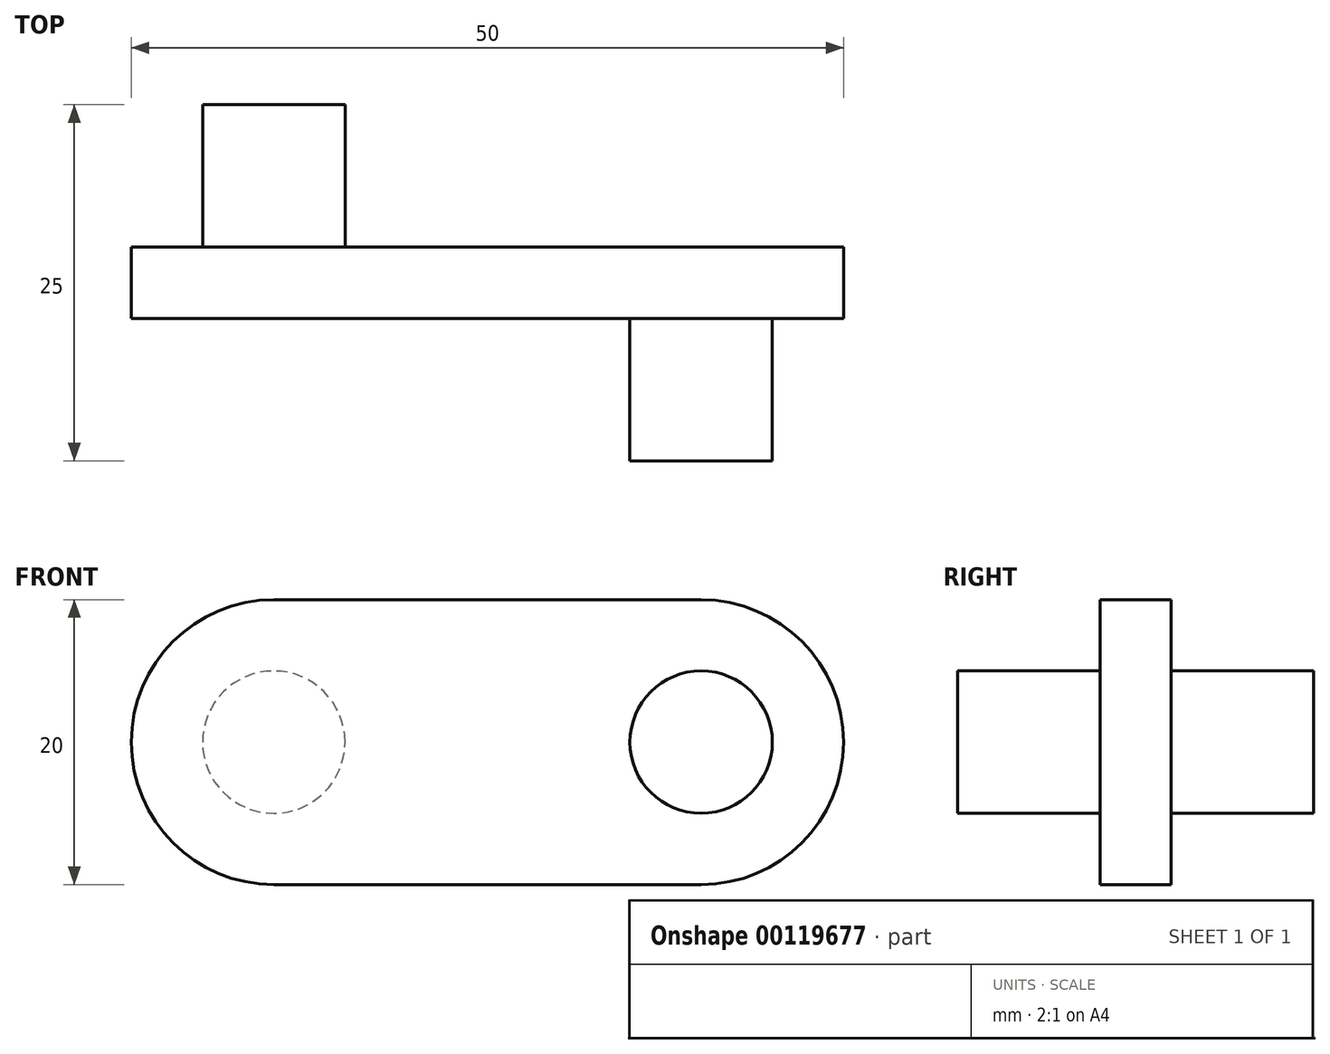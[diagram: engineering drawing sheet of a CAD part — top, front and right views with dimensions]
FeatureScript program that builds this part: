
annotation { "Feature Type Name" : "Feature", "Feature Type Description" : "" }
export const myFeature = defineFeature(function(context is Context, id is Id, definition is map)
    precondition{}
    {
        {
            var Q0;
            Q0=qCreatedBy(makeId("Front.planeOp"),FACE);
            var sketch = newSketch(context, id + "F0", { "sketchPlane" : qUnion([Q0])});
            skArc(sketch, "E0", {"start": v(0, 10) * mm, "mid": v(-10, 0) * mm, "end": v(0, -10) * mm});
            skLineSegment(sketch, "E1", {"start": v(0, 10) * mm, "end": v(30, 10) * mm});
            skLineSegment(sketch, "E2", {"start": v(0, -10) * mm, "end": v(30, -10) * mm});
            skArc(sketch, "E3", {"start": v(30, 10) * mm, "mid": v(40, 0) * mm, "end": v(30, -10) * mm});
            skSolve(sketch);
        }
        {
            var Q0;
            Q0=qSketchRegion(id+"F0",true);
            extrude(context, id + "F1", {"entities" : qUnion([Q0]), "endBound" : BoundingType.SYMMETRIC, "depth" : 5 * mm});
        }
        {
            var Q0;
            Q0=makeQuery(id+"F1.opExtrude","CAP_FACE",FACE,{"disambiguationData":[OSD([sQuery(id+"F0.wireOp",EDGE,"E0"),sQuery(id+"F0.wireOp",EDGE,"E1"),sQuery(id+"F0.wireOp",EDGE,"E2"),sQuery(id+"F0.wireOp",EDGE,"E3")])],"isStart":false});
            var sketch = newSketch(context, id + "F2", { "sketchPlane" : qUnion([Q0])});
            skCircle(sketch, "E4", {"center": v(30, 0) * mm, "radius": 5 * mm});
            skSolve(sketch);
        }
        {
            var Q0;
            Q0=qSketchRegion(id+"F2",true);
            extrude(context, id + "F3", {"entities" : qUnion([Q0]), "operationType" : NewBodyOperationType.ADD, "depth" : 10 * mm});
        }
        {
            var Q0;
            Q0=makeQuery(id+"F1.opExtrude","CAP_FACE",FACE,{"disambiguationData":[OSD([sQuery(id+"F0.wireOp",EDGE,"E0"),sQuery(id+"F0.wireOp",EDGE,"E1"),sQuery(id+"F0.wireOp",EDGE,"E2"),sQuery(id+"F0.wireOp",EDGE,"E3")])],"isStart":true});
            var sketch = newSketch(context, id + "F4", { "sketchPlane" : qUnion([Q0])});
            skCircle(sketch, "E5", {"center": v(0, 0) * mm, "radius": 5 * mm});
            skSolve(sketch);
        }
        {
            var Q0;
            Q0=qSketchRegion(id+"F4",true);
            extrude(context, id + "F5", {"entities" : qUnion([Q0]), "operationType" : NewBodyOperationType.ADD, "depth" : 10 * mm});
        }
    });
